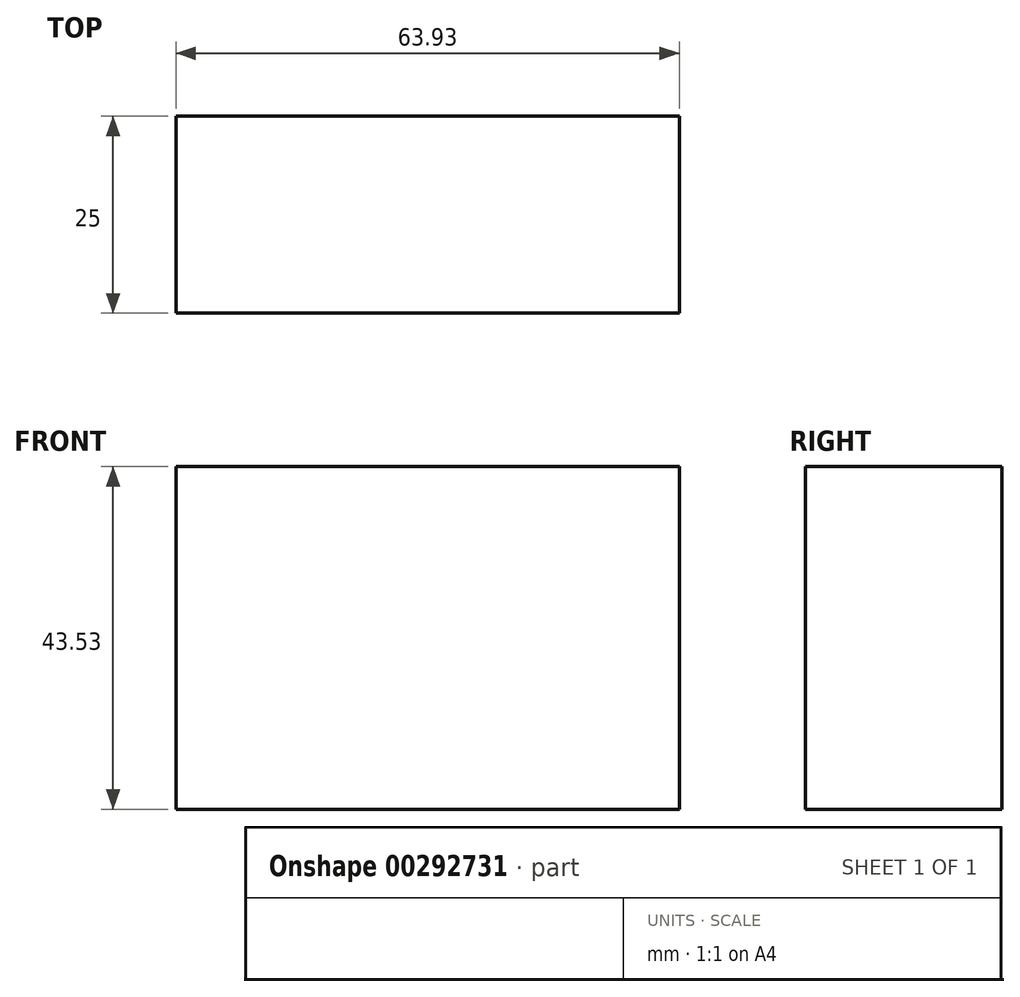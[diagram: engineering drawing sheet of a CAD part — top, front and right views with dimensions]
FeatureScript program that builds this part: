
annotation { "Feature Type Name" : "Feature", "Feature Type Description" : "" }
export const myFeature = defineFeature(function(context is Context, id is Id, definition is map)
    precondition{}
    {
        {
            var Q0;
            Q0=qCreatedBy(makeId("Front.planeOp"),FACE);
            var sketch = newSketch(context, id + "F0", { "sketchPlane" : qUnion([Q0])});
            skLineSegment(sketch, "E0.bottom", {"start": v(-121.38, 40.58) * mm, "end": v(-57.45, 40.58) * mm});
            skLineSegment(sketch, "E0.top", {"start": v(-121.38, -2.95) * mm, "end": v(-57.45, -2.95) * mm});
            skLineSegment(sketch, "E0.left", {"start": v(-121.38, 40.58) * mm, "end": v(-121.38, -2.95) * mm});
            skLineSegment(sketch, "E0.right", {"start": v(-57.45, 40.58) * mm, "end": v(-57.45, -2.95) * mm});
            skSolve(sketch);
        }
        {
            var Q0;
            Q0=makeQuery(id+"F0.imprint","IMPRINT",FACE,{"disambiguationData":[TD([[makeQuery(id+"F0.imprint","IMPRINT",EDGE,{"derivedFrom":sQuery(id+"F0.wireOp",EDGE,"E0.bottom")}),-1.0]])]});
            extrude(context, id + "F1", {"entities" : qUnion([Q0]), "depth" : 25 * mm});
        }
    });
